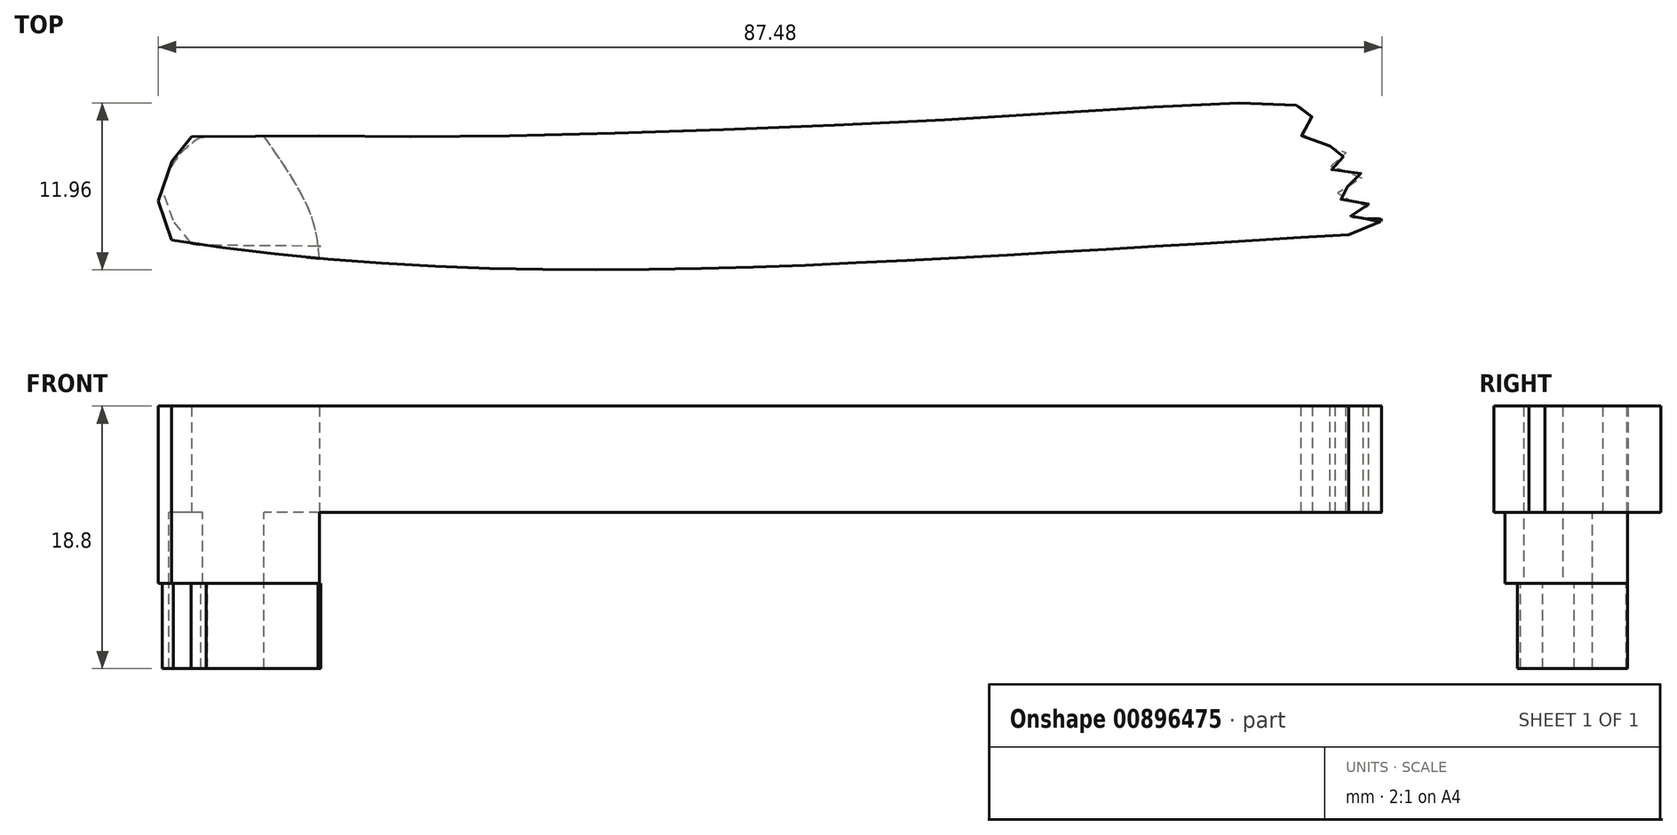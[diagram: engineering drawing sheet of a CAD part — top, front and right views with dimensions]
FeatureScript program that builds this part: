
annotation { "Feature Type Name" : "Feature", "Feature Type Description" : "" }
export const myFeature = defineFeature(function(context is Context, id is Id, definition is map)
    precondition{}
    {
        {
            var Q0;
            Q0=qCreatedBy(makeId("Top.planeOp"),FACE);
            var sketch = newSketch(context, id + "F0", { "sketchPlane" : qUnion([Q0])});
            skFitSpline(sketch, "E0", {"points": [v(47.98, 34.67) * mm, v(5.14, 30.61) * mm, v(-32.7, 22.37) * mm, v(-53.11, 13.18) * mm, v(-54.87, 3.04) * mm, v(-41.76, -5.07) * mm, v(-9.6, -9.4) * mm, v(24.06, -8.72) * mm, v(53.8, -6.96) * mm], "startDerivative": vector(-273.95, -18.17) * mm, "endDerivative": vector(223.68, 13.88) * mm});
            skFitSpline(sketch, "E1", {"points": [v(47.28, 24.7) * mm, v(9.51, 21.33) * mm, v(-30.24, 15.02) * mm, v(-45.34, 9.86) * mm, v(-38.56, 3.26) * mm, v(-13.8, 0) * mm, v(32.93, 1.73) * mm, v(50.42, 1.54) * mm, v(49.65, 0) * mm, v(52.8, -1.13) * mm, v(51.66, -2.28) * mm, v(54.05, -2.76) * mm, v(52.04, -4.29) * mm, v(54.43, -4.86) * mm, v(53, -5.82) * mm, v(55.3, -5.91) * mm, v(53, -7) * mm], "startDerivative": vector(-296, -20.83) * mm, "endDerivative": vector(-123.9, -44.97) * mm});
            skLineSegment(sketch, "E2", {"start": v(-20.59, 0.07) * mm, "end": v(-29.73, 0) * mm});
            skLineSegment(sketch, "E3", {"start": v(-29.73, 0) * mm, "end": v(-31.13, -1.76) * mm});
            skLineSegment(sketch, "E4", {"start": v(-31.13, -1.76) * mm, "end": v(-32.12, -4.6) * mm});
            skLineSegment(sketch, "E5", {"start": v(-32.12, -4.6) * mm, "end": v(-31.17, -7.4) * mm});
            skSolve(sketch);
        }
        {
            var Q0;
            Q0 = qSketchRegion(id + "F0", true);
            extrude(context, id + "F1", {"entities" : qUnion([Q0]), "depth" : 7.62 * mm, "offsetDistance" : 25.4 * mm});
        }
        {
            var Q0;
            Q0=makeQuery(id+"F1.opExtrude","CAP_FACE",FACE,{"disambiguationData":[OSD([sQuery(id+"F0.wireOp",EDGE,"E0"),sQuery(id+"F0.wireOp",EDGE,"E1"),sQuery(id+"F0.wireOp",EDGE,"E2"),sQuery(id+"F0.wireOp",EDGE,"E3"),sQuery(id+"F0.wireOp",EDGE,"E4"),sQuery(id+"F0.wireOp",EDGE,"E5")])],"isStart":true});
            var sketch = newSketch(context, id + "F2", { "sketchPlane" : qUnion([Q0])});
            skFitSpline(sketch, "E6", {"points": [v(-13.24, 9.24) * mm, v(-13.48, 6.15) * mm, v(-15.84, 4.88) * mm, v(-14.2, 2.29) * mm, v(-17.66, -0.01) * mm, v(-28.97, 0) * mm, v(-32.12, 4.6) * mm, v(-31.17, 7.4) * mm, v(-20.59, 8.72) * mm, v(-18.88, 8.86) * mm, v(-13.24, 9.24) * mm]});
            skPoint(sketch, "E7.2.internal.snap0", {"position": v(-25.16, -0.04) * mm});
            skFitSpline(sketch, "E7", {"points": [v(-20.59, 8.72) * mm, v(-21.3, 5.38) * mm, v(-25.16, -0.88) * mm], "startDerivative": vector(-0.8, -7.78) * mm, "endDerivative": vector(-7.9, -11.2) * mm});
            skSolve(sketch);
        }
        {
            var Q0;
            {var subQ0=makeQuery(id+"F1.opExtrude","CAP_EDGE",EDGE,{"disambiguationData":[OSD([sQuery(id+"F0.wireOp",EDGE,"E5")])],"isStart":true});Q0=makeQuery(id+"F2.imprint","IMPRINT",FACE,{"disambiguationData":[TD([[makeQuery(id+"F2.imprint","IMPRINT",EDGE,{"derivedFrom":subQ0}),-1.0]])]});}
            extrude(context, id + "F3", {"entities" : qUnion([Q0]), "operationType" : NewBodyOperationType.ADD, "depth" : 5.08 * mm, "offsetDistance" : 25.4 * mm});
        }
        {
            var Q0;
            Q0=makeQuery(id+"F3.opExtrude","CAP_FACE",FACE,{"disambiguationData":[OSD([sQuery(id+"F0.wireOp",EDGE,"E0"),sQuery(id+"F0.wireOp",EDGE,"E1"),sQuery(id+"F0.wireOp",EDGE,"E2"),sQuery(id+"F0.wireOp",EDGE,"E4"),sQuery(id+"F0.wireOp",EDGE,"E5"),sQuery(id+"F2.wireOp",EDGE,"E6")])],"isStart":false});
            var sketch = newSketch(context, id + "F4", { "sketchPlane" : qUnion([Q0])});
            skFitSpline(sketch, "E8", {"points": [v(48.04, 42.44) * mm, v(5.2, 38.39) * mm, v(-32.64, 30.14) * mm, v(-53.05, 20.95) * mm, v(-54.8, 10.82) * mm, v(-41.7, 2.7) * mm, v(-9.53, -1.62) * mm, v(24.12, -0.94) * mm, v(53.86, 0.81) * mm], "startDerivative": vector(-273.95, -18.17) * mm, "endDerivative": vector(223.68, 13.88) * mm});
            skFitSpline(sketch, "E9", {"points": [v(47.35, 32.47) * mm, v(9.58, 29.1) * mm, v(-30.18, 22.8) * mm, v(-45.28, 17.63) * mm, v(-38.5, 11.04) * mm, v(-13.74, 7.77) * mm, v(33, 9.5) * mm, v(50.48, 9.32) * mm, v(49.72, 7.77) * mm, v(52.87, 6.64) * mm, v(51.72, 5.5) * mm, v(54.11, 5.02) * mm, v(52.1, 3.49) * mm, v(54.5, 2.91) * mm, v(53.06, 1.96) * mm, v(55.36, 1.86) * mm, v(53.07, 0.77) * mm], "startDerivative": vector(-296, -20.83) * mm, "endDerivative": vector(-123.9, -44.97) * mm});
            skLineSegment(sketch, "E10", {"start": v(-20.52, 7.85) * mm, "end": v(-29.67, 7.77) * mm});
            skLineSegment(sketch, "E11", {"start": v(-29.67, 7.77) * mm, "end": v(-31.07, 6.02) * mm});
            skLineSegment(sketch, "E12", {"start": v(-31.07, 6.02) * mm, "end": v(-32.06, 3.17) * mm});
            skLineSegment(sketch, "E13", {"start": v(-32.06, 3.17) * mm, "end": v(-31.1, 0.37) * mm});
            skSolve(sketch);
        }
        {
            var Q0;
            {var subQ0=sQuery(id+"F0.wireOp",EDGE,"E1");var subQ1=makeQuery(id+"F3.opExtrude","CAP_EDGE",EDGE,{"disambiguationData":[OSD([subQ0])],"isStart":false});Q0=makeQuery(id+"F4.imprint","IMPRINT",FACE,{"disambiguationData":[TD([[makeQuery(id+"F4.imprint","IMPRINT",EDGE,{"derivedFrom":subQ1}),-1.0]])]});}
            var Q1;
            {var subQ2=sQuery(id+"F0.wireOp",EDGE,"E1");var subQ3=makeQuery(id+"F3.opExtrude","CAP_EDGE",EDGE,{"disambiguationData":[OSD([subQ2])],"isStart":false});Q1=makeQuery(id+"F4.imprint","IMPRINT",FACE,{"disambiguationData":[TD([[makeQuery(id+"F4.imprint","IMPRINT",EDGE,{"derivedFrom":subQ3}),1.0]])]});}
            var Q2;
            {var subQ13=sQuery(id+"F4.wireOp",EDGE,"E8");var subQ14=makeQuery(id+"F3.opExtrude","CAP_EDGE",EDGE,{"disambiguationData":[OSD([sQuery(id+"F2.wireOp",EDGE,"E6")])],"isStart":false});var subQ15=makeQuery(id+"F4.imprint","INTERSECT",VERTEX,{"derivedFrom":[subQ14,subQ13]});Q2=makeQuery(id+"F4.imprint","IMPRINT",FACE,{"disambiguationData":[TD([[makeQuery(id+"F4.imprint","IMPRINT",EDGE,{"disambiguationData":[TD([[subQ15,-1.0]])],"derivedFrom":subQ13}),1.0]])]});}
            var Q3;
            {var subQ5=sQuery(id+"F4.wireOp",EDGE,"E9");Q3=makeQuery(id+"F4.imprint","IMPRINT",FACE,{"disambiguationData":[TD([[makeQuery(id+"F4.imprint","IMPRINT",EDGE,{"derivedFrom":subQ5}),-1.0]])]});}
            extrude(context, id + "F5", {"entities" : qUnion([Q0, Q1, Q2, Q3]), "depth" : 6.1 * mm, "offsetDistance" : 25.4 * mm});
        }
    });
